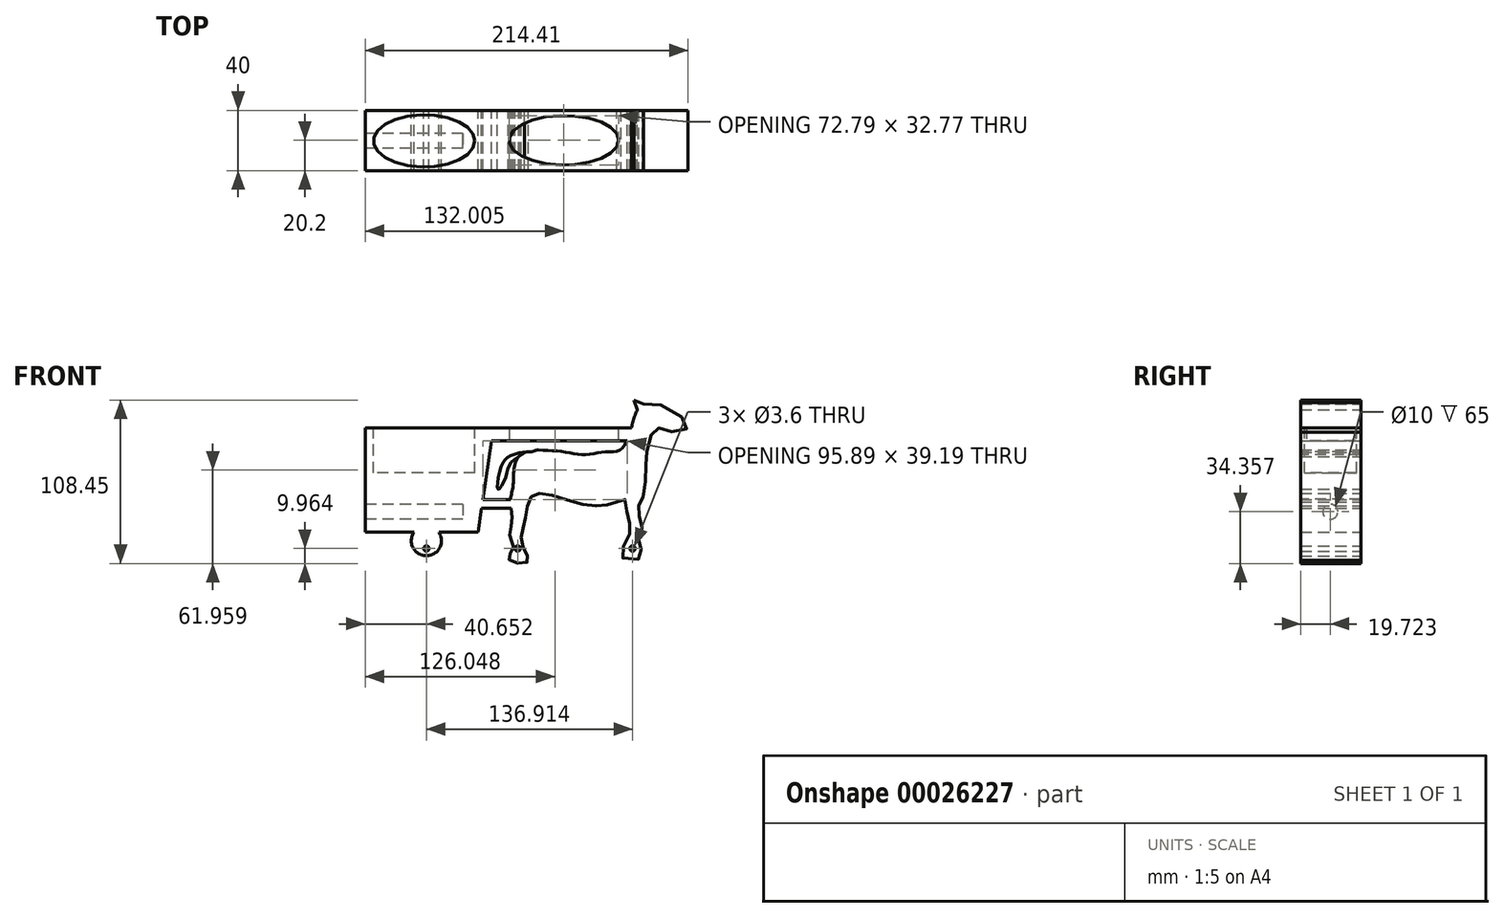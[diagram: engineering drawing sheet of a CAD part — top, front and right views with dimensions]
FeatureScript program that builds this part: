
annotation { "Feature Type Name" : "Feature", "Feature Type Description" : "" }
export const myFeature = defineFeature(function(context is Context, id is Id, definition is map)
    precondition{}
    {
        {
            var Q0;
            Q0=qCreatedBy(makeId("Front.planeOp"),FACE);
            var sketch = newSketch(context, id + "F0", { "sketchPlane" : qUnion([Q0])});
            skLineSegment(sketch, "E0", {"start": v(0, -76.92) * mm, "end": v(10, -7.64) * mm});
            skLineSegment(sketch, "E1", {"start": v(10, -7.64) * mm, "end": v(-75, -7.64) * mm});
            skLineSegment(sketch, "E2", {"start": v(10, -7.64) * mm, "end": v(72.01, -7.64) * mm});
            skFitSpline(sketch, "E3", {"points": [v(38.4, -22.32) * mm, v(30.76, -23.98) * mm, v(24.8, -30.76) * mm, v(23.48, -41.92) * mm, v(22.9, -48.38) * mm, v(21.52, -56.07) * mm, v(22.53, -68.95) * mm, v(21.27, -81.2) * mm, v(23.53, -86.85) * mm, v(20.32, -94.9) * mm, v(32.79, -96.7) * mm, v(29.17, -84.64) * mm, v(31.18, -68.75) * mm, v(37.2, -51.88) * mm, v(70.34, -58.69) * mm, v(92.03, -57.06) * mm], "startDerivative": vector(-127.41, -111.11) * mm, "endDerivative": vector(184.82, 67.14) * mm});
            skFitSpline(sketch, "E4", {"points": [v(38.4, -22.32) * mm, v(56.24, -23.44) * mm, v(70.07, -25.6) * mm, v(83.36, -23.71) * mm, v(94.47, -22.32) * mm, v(101.52, -8.8) * mm, v(105.86, 4.22) * mm, v(116.43, 8.82) * mm, v(139.41, -6.6) * mm, v(127.55, -10.15) * mm, v(117.8, -7.99) * mm, v(112.37, -22.32) * mm, v(111.28, -35.64) * mm, v(109.66, -53.8) * mm, v(106.67, -58.96) * mm, v(107.22, -66.55) * mm, v(108.57, -76.04) * mm, v(106.13, -83.36) * mm, v(108.84, -93.4) * mm, v(95.56, -93.66) * mm, v(98.54, -82.82) * mm, v(101.25, -74.14) * mm, v(98.81, -64.38) * mm, v(97.46, -55.16) * mm, v(92.03, -57.06) * mm], "startDerivative": vector(349.51, -32.67) * mm, "endDerivative": vector(-228.9, -138.23) * mm});
            skLineSegment(sketch, "E5", {"start": v(105.86, 4.22) * mm, "end": v(103.48, 10.68) * mm});
            skLineSegment(sketch, "E6", {"start": v(103.48, 10.68) * mm, "end": v(109.98, 8.15) * mm});
            skLineSegment(sketch, "E7", {"start": v(72.01, -7.64) * mm, "end": v(101.52, -7.64) * mm});
            skLineSegment(sketch, "E8", {"start": v(8.76, -16.22) * mm, "end": v(99, -16.22) * mm});
            skLineSegment(sketch, "E9", {"start": v(101.52, -7.64) * mm, "end": v(112.4, -7.64) * mm});
            skLineSegment(sketch, "E10", {"start": v(112.4, -8.1) * mm, "end": v(112.4, -16.22) * mm});
            skLineSegment(sketch, "E11", {"start": v(99, -16.22) * mm, "end": v(112.4, -16.22) * mm});
            skFitSpline(sketch, "E12", {"points": [v(30.76, -23.98) * mm, v(21.94, -26.02) * mm, v(15.32, -33.55) * mm, v(13.27, -48.37) * mm, v(18.29, -40.62) * mm, v(22.62, -30.13) * mm, v(30.76, -23.98) * mm]});
            skLineSegment(sketch, "E13", {"start": v(-75, -7.64) * mm, "end": v(-75, -76.92) * mm});
            skLineSegment(sketch, "E14", {"start": v(-75, -76.92) * mm, "end": v(0, -76.92) * mm});
            skLineSegment(sketch, "E15", {"start": v(3.1, -55.4) * mm, "end": v(22.9, -55.4) * mm});
            skLineSegment(sketch, "E16", {"start": v(2.29, -61.07) * mm, "end": v(21.97, -61.07) * mm});
            skSolve(sketch);
        }
        {
            var Q0;
            {var subQ1=sQuery(id+"F0.wireOp",EDGE,"E3");var subQ4=sQuery(id+"F0.wireOp",EDGE,"E4");var subQ10=makeQuery(id+"F0.imprint","INTERSECT",VERTEX,{"disambiguationData":[OD(0.0)],"derivedFrom":[subQ1,subQ4]});Q0=makeQuery(id+"F0.imprint","IMPRINT",FACE,{"disambiguationData":[TD([[makeQuery(id+"F0.imprint","IMPRINT",EDGE,{"disambiguationData":[TD([[subQ10,-1.0]])],"derivedFrom":subQ1}),1.0]])]});}
            var sketch = newSketch(context, id + "F1", { "sketchPlane" : qUnion([Q0])});
            skCircle(sketch, "E17", {"center": v(102.57, -87.8) * mm, "radius": 1.8 * mm});
            skCircle(sketch, "E18", {"center": v(26.33, -87.8) * mm, "radius": 1.8 * mm});
            skCircle(sketch, "E19", {"center": v(-34.35, -82.68) * mm, "radius": 10.02 * mm});
            skCircle(sketch, "E20", {"center": v(-34.35, -87.8) * mm, "radius": 1.8 * mm});
            skSolve(sketch);
        }
        {
            var Q0;
            {var subQ1=sQuery(id+"F0.wireOp",EDGE,"E3");var subQ4=sQuery(id+"F0.wireOp",EDGE,"E4");var subQ10=makeQuery(id+"F0.imprint","INTERSECT",VERTEX,{"disambiguationData":[OD(0.0)],"derivedFrom":[subQ1,subQ4]});Q0=makeQuery(id+"F0.imprint","IMPRINT",FACE,{"disambiguationData":[TD([[makeQuery(id+"F0.imprint","IMPRINT",EDGE,{"disambiguationData":[TD([[subQ10,-1.0]])],"derivedFrom":subQ1}),1.0]])]});}
            var Q1;
            {var subQ1=sQuery(id+"F0.wireOp",EDGE,"E1");Q1=makeQuery(id+"F0.imprint","IMPRINT",FACE,{"disambiguationData":[TD([[makeQuery(id+"F0.imprint","IMPRINT",EDGE,{"derivedFrom":subQ1}),1.0]])]});}
            var Q2;
            {var subQ5=sQuery(id+"F0.wireOp",EDGE,"E2");Q2=makeQuery(id+"F0.imprint","IMPRINT",FACE,{"disambiguationData":[TD([[makeQuery(id+"F0.imprint","IMPRINT",EDGE,{"derivedFrom":subQ5}),-1.0]])]});}
            extrude(context, id + "F2", {"entities" : qUnion([Q0, Q1, Q2]), "depth" : 40 * mm});
        }
        {
            var Q0;
            {var subQ0=sQuery(id+"F0.wireOp",EDGE,"E12");var subQ1=sQuery(id+"F0.wireOp",EDGE,"E3");var subQ3=makeQuery(id+"F0.imprint","INTERSECT",VERTEX,{"disambiguationData":[OD(0.0)],"derivedFrom":[subQ1,subQ0]});Q0=makeQuery(id+"F0.imprint","IMPRINT",FACE,{"disambiguationData":[TD([[makeQuery(id+"F0.imprint","IMPRINT",EDGE,{"disambiguationData":[TD([[subQ3,-1.0]])],"derivedFrom":subQ1}),-1.0]])]});}
            var Q1;
            {var subQ1=sQuery(id+"F0.wireOp",EDGE,"E5");Q1=makeQuery(id+"F0.imprint","IMPRINT",FACE,{"disambiguationData":[TD([[makeQuery(id+"F0.imprint","IMPRINT",EDGE,{"derivedFrom":subQ1}),-1.0]])]});}
            var Q2;
            Q2=makeQuery(id+"F1.imprint","IMPRINT",FACE,{"disambiguationData":[TD([[makeQuery(id+"F1.imprint","IMPRINT",EDGE,{"derivedFrom":sQuery(id+"F1.wireOp",EDGE,"E19")}),1.0]])]});
            extrude(context, id + "F3", {"entities" : qUnion([Q0, Q1, Q2]), "operationType" : NewBodyOperationType.ADD, "depth" : 40 * mm});
        }
        {
            var Q0;
            {var subQ0=sQuery(id+"F0.wireOp",EDGE,"E12");var subQ1=sQuery(id+"F0.wireOp",EDGE,"E3");var subQ3=makeQuery(id+"F0.imprint","INTERSECT",VERTEX,{"disambiguationData":[OD(0.0)],"derivedFrom":[subQ1,subQ0]});Q0=makeQuery(id+"F0.imprint","IMPRINT",FACE,{"disambiguationData":[TD([[makeQuery(id+"F0.imprint","IMPRINT",EDGE,{"disambiguationData":[TD([[subQ3,-1.0]])],"derivedFrom":subQ1}),1.0]])]});}
            extrude(context, id + "F4", {"entities" : qUnion([Q0]), "depth" : 40 * mm});
        }
        {
            var Q0;
            Q0=makeQuery(id+"F1.imprint","IMPRINT",FACE,{"disambiguationData":[TD([[makeQuery(id+"F1.imprint","IMPRINT",EDGE,{"derivedFrom":sQuery(id+"F1.wireOp",EDGE,"E17")}),1.0]])]});
            extrude(context, id + "F5", {"entities" : qUnion([Q0]), "operationType" : NewBodyOperationType.REMOVE, "endBound" : BoundingType.THROUGH_ALL, "depth" : 25 * mm});
        }
        {
            var Q0;
            Q0=makeQuery(id+"F1.imprint","IMPRINT",FACE,{"disambiguationData":[TD([[makeQuery(id+"F1.imprint","IMPRINT",EDGE,{"derivedFrom":sQuery(id+"F1.wireOp",EDGE,"E18")}),1.0]])]});
            extrude(context, id + "F6", {"entities" : qUnion([Q0]), "operationType" : NewBodyOperationType.REMOVE, "endBound" : BoundingType.THROUGH_ALL, "depth" : 25 * mm});
        }
        {
            var Q0;
            Q0=makeQuery(id+"F2.opExtrude","SWEPT_FACE",FACE,{"disambiguationData":[OSD([sQuery(id+"F0.wireOp",EDGE,"E13")])]});
            var sketch = newSketch(context, id + "F7", { "sketchPlane" : qUnion([Q0])});
            skCircle(sketch, "E21", {"center": v(20.28, -63.41) * mm, "radius": 5 * mm});
            skSolve(sketch);
        }
        {
            var Q0;
            Q0=makeQuery(id+"F7.imprint","IMPRINT",FACE,{"disambiguationData":[TD([[makeQuery(id+"F7.imprint","IMPRINT",EDGE,{"derivedFrom":sQuery(id+"F7.wireOp",EDGE,"E21")}),1.0]])]});
            extrude(context, id + "F8", {"entities" : qUnion([Q0]), "operationType" : NewBodyOperationType.REMOVE, "oppositeDirection" : true, "depth" : 65 * mm});
        }
        {
            var Q0;
            {var subQ0=sQuery(id+"F0.wireOp",EDGE,"E16");Q0=makeQuery(id+"F0.imprint","IMPRINT",FACE,{"disambiguationData":[TD([[makeQuery(id+"F0.imprint","IMPRINT",EDGE,{"derivedFrom":subQ0}),1.0]])]});}
            extrude(context, id + "F9", {"entities" : qUnion([Q0]), "operationType" : NewBodyOperationType.ADD, "depth" : 40 * mm});
        }
        {
            var Q0;
            Q0=makeQuery(id+"F2.opExtrude","SWEPT_FACE",FACE,{"disambiguationData":[OSD([sQuery(id+"F0.wireOp",EDGE,"E1"),sQuery(id+"F0.wireOp",EDGE,"E2"),sQuery(id+"F0.wireOp",EDGE,"E7"),sQuery(id+"F0.wireOp",EDGE,"E9")])]});
            var sketch = newSketch(context, id + "F10", { "sketchPlane" : qUnion([Q0])});
            skEllipse(sketch, "E22", {"center": v(57, -19.8) * mm, "majorRadius": 36.4 * mm, "minorRadius": 16.39 * mm, "majorAxis": v(1, 0)});
            skSolve(sketch);
        }
        {
            var Q0;
            Q0=makeQuery(id+"F10.imprint","IMPRINT",FACE,{"disambiguationData":[TD([[makeQuery(id+"F10.imprint","IMPRINT",EDGE,{"derivedFrom":sQuery(id+"F10.wireOp",EDGE,"E22")}),1.0]])]});
            extrude(context, id + "F11", {"entities" : qUnion([Q0]), "operationType" : NewBodyOperationType.REMOVE, "oppositeDirection" : true, "depth" : 14 * mm});
        }
        {
            var Q0;
            Q0=makeQuery(id+"F10.imprint","IMPRINT",FACE,{"disambiguationData":[TD([[makeQuery(id+"F10.imprint","IMPRINT",EDGE,{"derivedFrom":sQuery(id+"F10.wireOp",EDGE,"E22")}),-1.0]])]});
            var sketch = newSketch(context, id + "F12", { "sketchPlane" : qUnion([Q0])});
            skEllipse(sketch, "E23", {"center": v(-35.78, -20.23) * mm, "majorRadius": 33.73 * mm, "minorRadius": 17.3 * mm, "majorAxis": v(1, 0)});
            skSolve(sketch);
        }
        {
            var Q0;
            Q0=makeQuery(id+"F12.imprint","IMPRINT",FACE,{"disambiguationData":[TD([[makeQuery(id+"F12.imprint","IMPRINT",EDGE,{"derivedFrom":sQuery(id+"F12.wireOp",EDGE,"E23")}),1.0]])]});
            extrude(context, id + "F13", {"entities" : qUnion([Q0]), "operationType" : NewBodyOperationType.REMOVE, "oppositeDirection" : true, "depth" : 30 * mm});
        }
        {
            var Q0;
            {var subQ0=sQuery(id+"F0.wireOp",EDGE,"E3");var subQ1=sQuery(id+"F0.wireOp",EDGE,"E4");Q0=makeQuery(id+"F2.opExtrude","SWEPT_EDGE",EDGE,{"disambiguationData":[OSD([subQ0,subQ1]),TDD([makeQuery(id+"F0.imprint","INTERSECT",VERTEX,{"disambiguationData":[OD(0.0)],"derivedFrom":[subQ0,subQ1]})])]});}
            fillet(context, id + "F14", {"entities" : qUnion([Q0]), "radius" : 5 * mm, "tangentPropagation" : true, "allowEdgeOverflow" : false});
        }
    });
